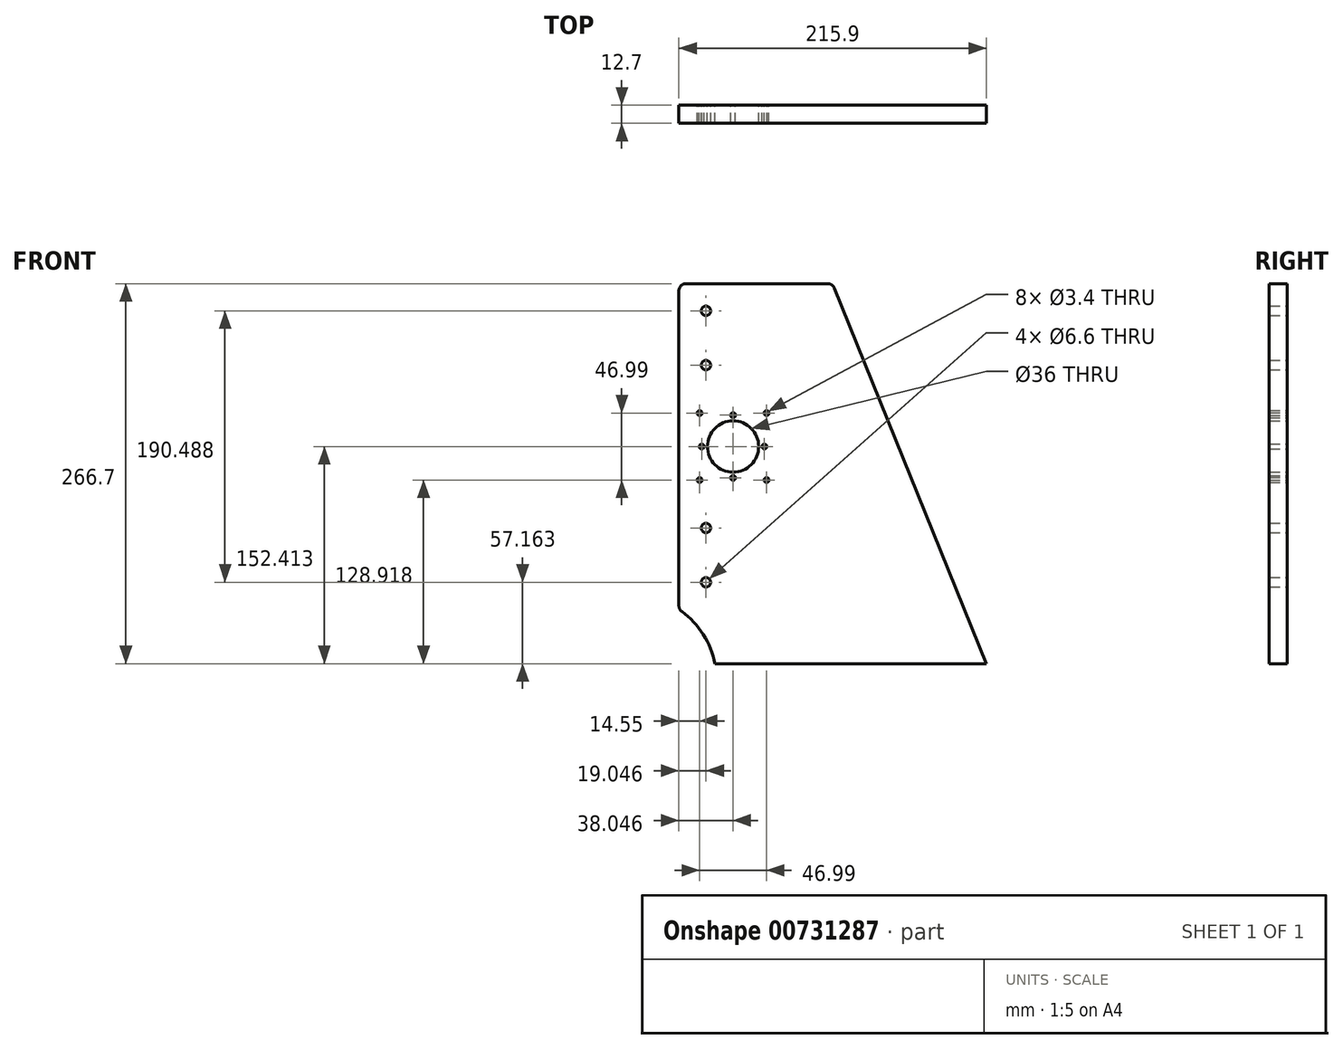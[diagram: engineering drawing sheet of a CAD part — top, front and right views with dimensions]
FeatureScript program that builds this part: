
annotation { "Feature Type Name" : "Feature", "Feature Type Description" : "" }
export const myFeature = defineFeature(function(context is Context, id is Id, definition is map)
    precondition{}
    {
        {
            var Q0;
            Q0=qCreatedBy(makeId("Front.planeOp"),FACE);
            var sketch = newSketch(context, id + "F0", { "sketchPlane" : qUnion([Q0])});
            skLineSegment(sketch, "E0.bottom", {"start": v(108.43, 152.4) * mm, "end": v(-107.47, 152.4) * mm});
            skLineSegment(sketch, "E0.left", {"start": v(108.43, 152.4) * mm, "end": v(108.43, -114.3) * mm});
            skLineSegment(sketch, "E0.right", {"start": v(-107.47, 152.4) * mm, "end": v(-107.47, -114.3) * mm});
            skPoint(sketch, "E0.middle", {"position": v(0, 0) * mm});
            skCircle(sketch, "E1", {"center": v(-88.42, -57.14) * mm, "radius": 3.3 * mm});
            skCircle(sketch, "E2", {"center": v(-88.42, -19.04) * mm, "radius": 3.3 * mm});
            skCircle(sketch, "E3", {"center": v(-88.42, 95.25) * mm, "radius": 3.3 * mm});
            skCircle(sketch, "E4", {"center": v(-88.42, 133.35) * mm, "radius": 3.3 * mm});
            skLineSegment(sketch, "E5", {"start": v(32.23, 152.4) * mm, "end": v(108.43, 0) * mm});
            skLineSegment(sketch, "E6", {"start": v(-107.47, -114.3) * mm, "end": v(108.43, -114.3) * mm});
            skLineSegment(sketch, "E7", {"start": v(-107.47, -76.2) * mm, "end": v(108.43, -76.2) * mm, "construction": true});
            skPoint(sketch, "E8.middle", {"position": v(-69.42, 38.11) * mm});
            skLineSegment(sketch, "E9", {"start": v(-69.42, 74.31) * mm, "end": v(-69.42, 11.11) * mm, "construction": true});
            skPoint(sketch, "E10.startSnap0", {"position": v(0.48, 152.4) * mm});
            skCircle(sketch, "E11", {"center": v(-69.42, 38.11) * mm, "radius": 18 * mm});
            skLineSegment(sketch, "E12", {"start": v(-98.77, 38.11) * mm, "end": v(-40.23, 38.11) * mm, "construction": true});
            skLineSegment(sketch, "E13", {"start": v(-91.1, 59.79) * mm, "end": v(-42.84, 11.53) * mm, "construction": true});
            skLineSegment(sketch, "E14", {"start": v(-49.22, 58.32) * mm, "end": v(-94.15, 13.39) * mm, "construction": true});
            skCircle(sketch, "E15", {"center": v(-92.92, 61.6) * mm, "radius": 1.7 * mm});
            skCircle(sketch, "E16.MirrorC", {"center": v(-92.92, 14.62) * mm, "radius": 1.7 * mm});
            skCircle(sketch, "E17.MirrorC", {"center": v(-45.93, 61.6) * mm, "radius": 1.7 * mm});
            skCircle(sketch, "E18.MirrorC", {"center": v(-45.93, 14.62) * mm, "radius": 1.7 * mm});
            skCircle(sketch, "E19", {"center": v(-69.42, 60.11) * mm, "radius": 1.7 * mm});
            skCircle(sketch, "E20.MirrorC", {"center": v(-69.42, 16.11) * mm, "radius": 1.7 * mm});
            skCircle(sketch, "E21", {"center": v(-91.42, 38.11) * mm, "radius": 1.7 * mm});
            skCircle(sketch, "E22.MirrorC", {"center": v(-47.42, 38.11) * mm, "radius": 1.7 * mm});
            skLineSegment(sketch, "E23", {"start": v(0.48, 152.4) * mm, "end": v(108.43, -114.3) * mm});
            skArc(sketch, "E24", {"start": v(-82.07, -114.3) * mm, "mid": v(-91.1, -92.8) * mm, "end": v(-107.47, -76.2) * mm});
            skSolve(sketch);
        }
        {
            var Q0;
            Q0=makeQuery(id+"F0.imprint","IMPRINT",FACE,{"disambiguationData":[TD([[makeQuery(id+"F0.imprint","IMPRINT",EDGE,{"derivedFrom":sQuery(id+"F0.wireOp",EDGE,"E1")}),-1.0]])]});
            extrude(context, id + "F1", {"entities" : qUnion([Q0]), "depth" : 12.7 * mm, "offsetDistance" : 25.4 * mm});
        }
        {
            var Q0;
            Q0=makeQuery(id+"F1.opExtrude","SWEPT_EDGE",EDGE,{"disambiguationData":[OSD([sQuery(id+"F0.wireOp",EDGE,"E0.bottom"),sQuery(id+"F0.wireOp",EDGE,"E23")])]});
            var Q1;
            Q1=makeQuery(id+"F1.opExtrude","SWEPT_EDGE",EDGE,{"disambiguationData":[OSD([sQuery(id+"F0.wireOp",EDGE,"E0.bottom"),sQuery(id+"F0.wireOp",EDGE,"E0.right")])]});
            var Q2;
            Q2=makeQuery(id+"F1.opExtrude","SWEPT_EDGE",EDGE,{"disambiguationData":[OSD([sQuery(id+"F0.wireOp",EDGE,"E0.right"),sQuery(id+"F0.wireOp",EDGE,"E24")])]});
            fillet(context, id + "F2", {"entities" : qUnion([Q0, Q1, Q2]), "radius" : 5.08 * mm, "tangentPropagation" : true, "allowEdgeOverflow" : false});
        }
    });
